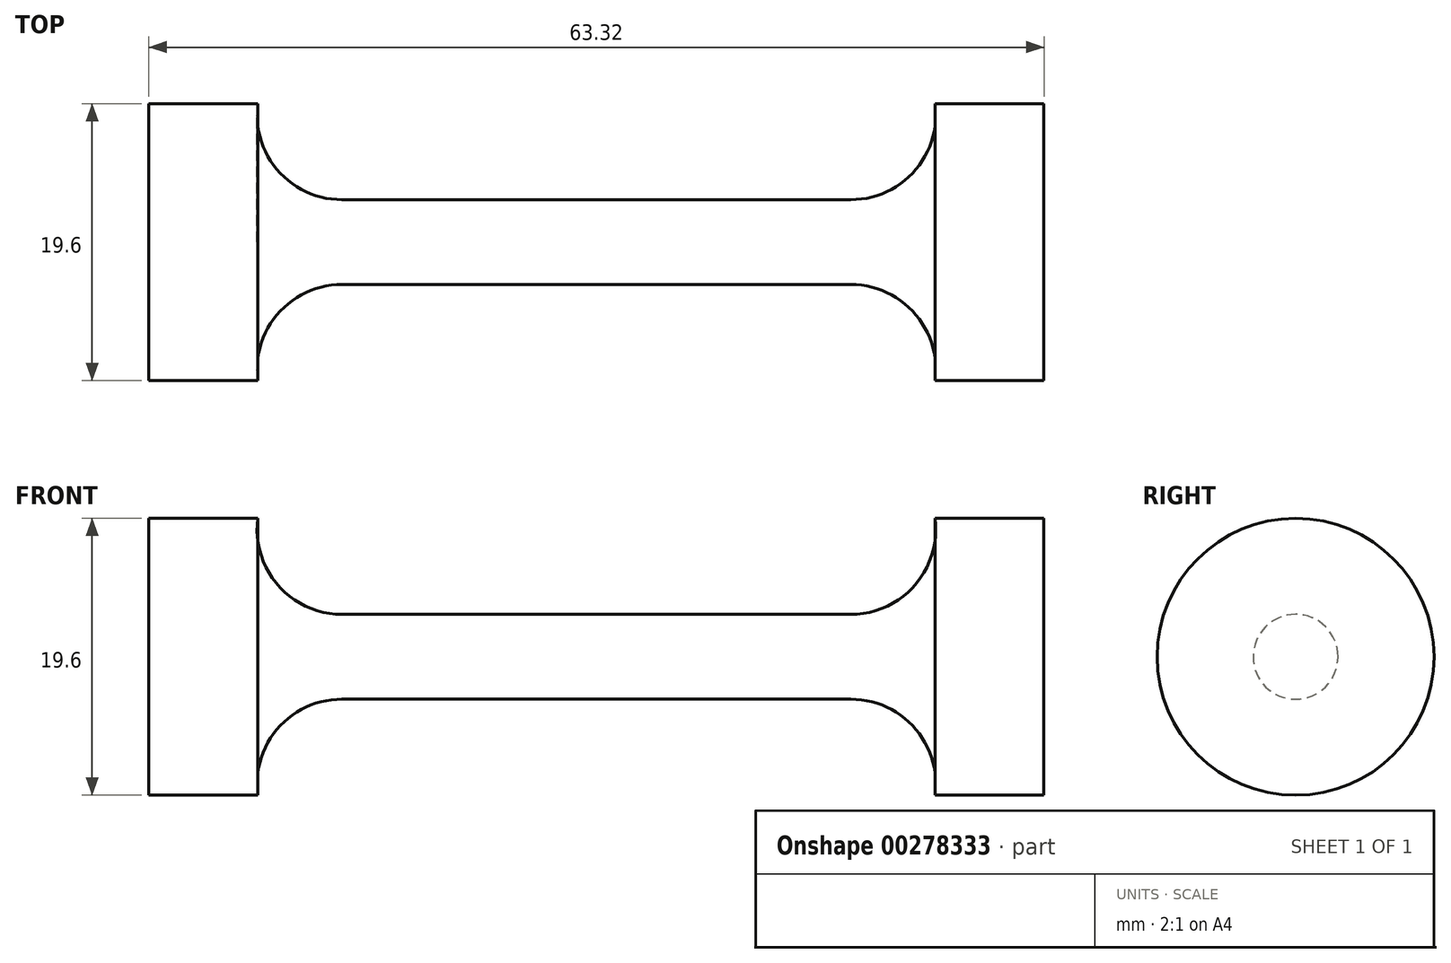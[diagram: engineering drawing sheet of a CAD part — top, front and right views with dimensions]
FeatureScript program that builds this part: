
annotation { "Feature Type Name" : "Feature", "Feature Type Description" : "" }
export const myFeature = defineFeature(function(context is Context, id is Id, definition is map)
    precondition{}
    {
        {
            var Q0;
            Q0=qCreatedBy(makeId("Front.planeOp"),FACE);
            var sketch = newSketch(context, id + "F0", { "sketchPlane" : qUnion([Q0])});
            skLineSegment(sketch, "E0", {"start": v(0, 3) * mm, "end": v(18, 3) * mm});
            skArc(sketch, "E1", {"start": v(18, 3) * mm, "mid": v(22.52, 5.05) * mm, "end": v(23.95, 9.8) * mm});
            skLineSegment(sketch, "E2", {"start": v(23.95, 9.8) * mm, "end": v(31.66, 9.8) * mm});
            skLineSegment(sketch, "E3", {"start": v(31.66, 9.8) * mm, "end": v(31.66, 0) * mm});
            skLineSegment(sketch, "E4.MirrorCS", {"start": v(0, 3) * mm, "end": v(-18, 3) * mm});
            skLineSegment(sketch, "E5.MirrorCS", {"start": v(-31.66, 9.8) * mm, "end": v(-31.66, 0) * mm});
            skLineSegment(sketch, "E6.MirrorCS", {"start": v(-23.95, 9.8) * mm, "end": v(-31.66, 9.8) * mm});
            skArc(sketch, "E7.MirrorCS", {"start": v(-18, 3) * mm, "mid": v(-22.52, 5.05) * mm, "end": v(-23.95, 9.8) * mm});
            skLineSegment(sketch, "E8", {"start": v(-31.66, 0) * mm, "end": v(31.66, 0) * mm});
            skSolve(sketch);
        }
        {
            var Q0;
            Q0 = qSketchRegion(id + "F0", true);
            var Q1;
            Q1=sQuery(id+"F0.wireOp",EDGE,"E8");
            revolve(context, id + "F1", {"entities" : qUnion([Q0]), "axis" : qUnion([Q1]), "revolveType" : RevolveType.FULL});
        }
    });
